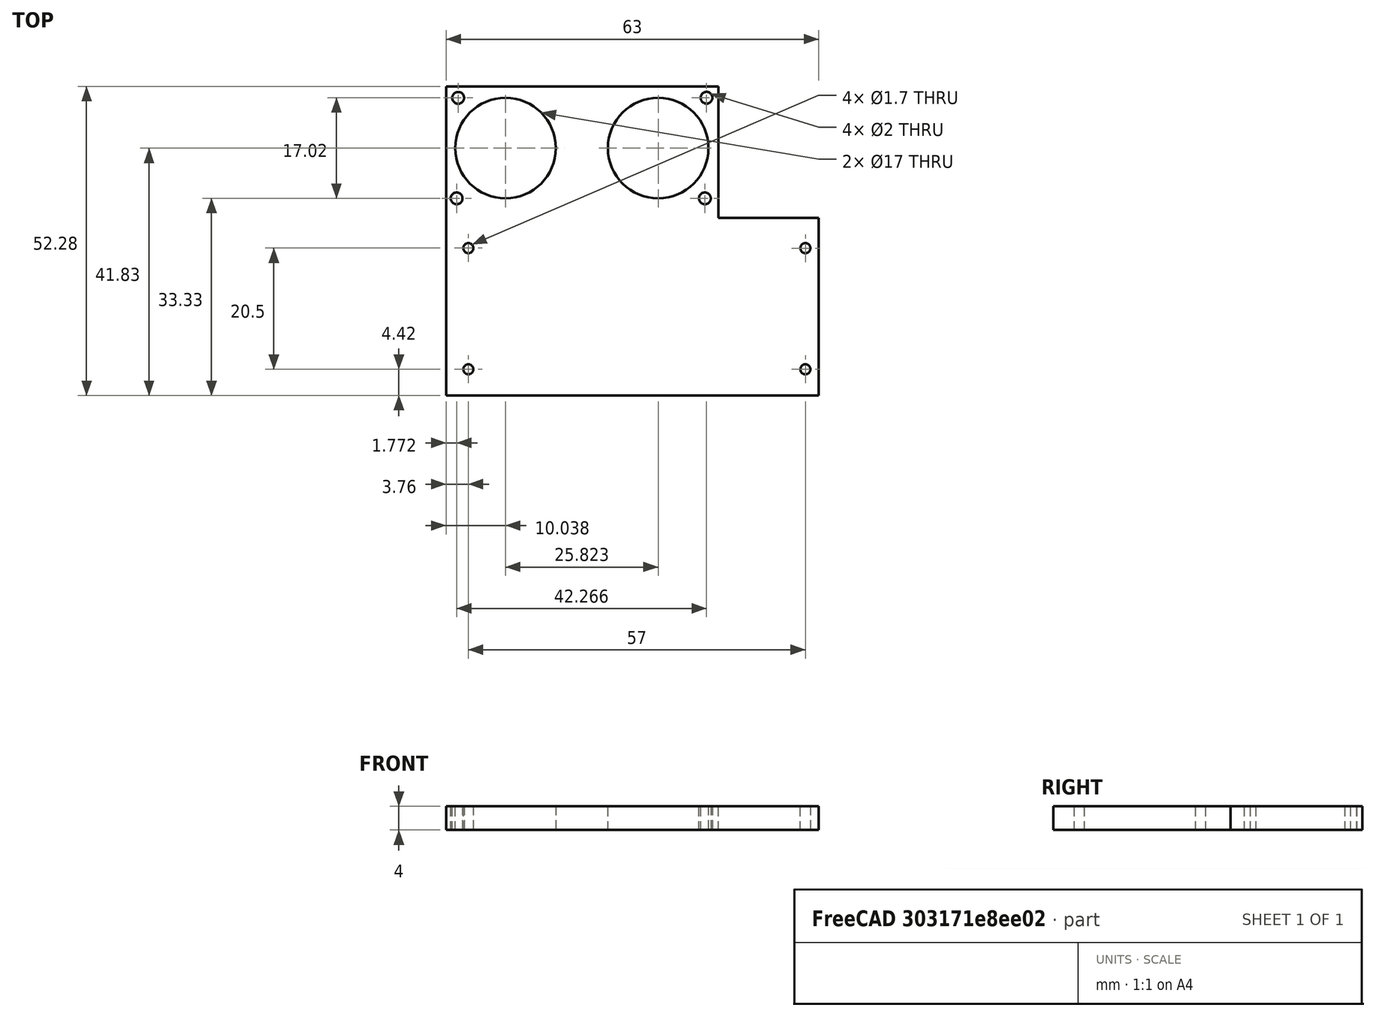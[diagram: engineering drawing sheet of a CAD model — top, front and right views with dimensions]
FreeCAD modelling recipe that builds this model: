
FCSTD DOCUMENT  (FreeCAD 1.0RUnknown)
Label: ultrasonic_holder
License: All rights reserved
LicenseURL: https://en.wikipedia.org/wiki/All_rights_reserved
objects: Sketcher::SketchObject×3, PartDesign::Pocket×2, Mesh::Feature×1, PartDesign::Pad×1, PartDesign::Body×1
note: 16 computed .brp shape members not serialized (recipe doc carries the construction recipe); baked Part::Feature solids carry a one-line shape summary decoded from their .brp

FEATURE [Mesh::Feature] ultrasonic_holder_v3  label="ultrasonic holder v3"
FEATURE [Sketcher::SketchObject] Sketch
  ArcFitTolerance = 1e-06
  FullyConstrained = false
  MakeInternals = false
  sketch-geometry (9):
    g0: LineSegment StartX=-1.10876 StartY=-16.1017 StartZ=0 EndX=-1.10876 EndY=-25.1017 EndZ=0
    g1: LineSegment StartX=-1.10876 StartY=-25.1017 StartZ=0 EndX=34.8912 EndY=-25.1017 EndZ=0
    g2: LineSegment StartX=34.8912 StartY=-25.1017 StartZ=0 EndX=34.8912 EndY=-16.1017 EndZ=0
    g3: LineSegment StartX=34.8912 StartY=-16.1017 StartZ=0 EndX=-1.10876 EndY=-16.1017 EndZ=0
    g4: LineSegment StartX=-1.32171 StartY=-38.5763 StartZ=0 EndX=34.9013 EndY=-38.5763 EndZ=0
    g5: LineSegment StartX=34.9013 StartY=-29.5763 StartZ=0 EndX=-1.32171 EndY=-29.5763 EndZ=0
    g6: LineSegment StartX=-1.32171 StartY=-38.5763 StartZ=0 EndX=-1.32171 EndY=-29.5763 EndZ=0
    g7: LineSegment StartX=-1.10876 StartY=-25.1017 StartZ=0 EndX=34.8912 EndY=-25.1017 EndZ=0
    g8: LineSegment StartX=34.9013 StartY=-29.5763 StartZ=0 EndX=34.9013 EndY=-38.5763 EndZ=0
  constraints (18):
    c: Vertical(g0)
    c: Vertical(g2)
    c: Horizontal(g1)
    c: Horizontal(g3)
    c: Distance(g0,g2) = 36
    c: Distance(g1,g3) = 9
    c: Horizontal(g4)
    c: Horizontal(g5)
    c: Distance(g4,g5) = 9
    c: Coincident(g6,g4)
    c: Coincident(g6,g5)
    c: Vertical(g6)
    c: Coincident(g7,g0)
    c: Coincident(g7,g2)
    c: Horizontal(g7)
    c: Coincident(g8,g5)
    c: Coincident(g8,g4)
    c: Vertical(g8)
FEATURE [Sketcher::SketchObject] Sketch001
  ArcFitTolerance = 1e-06
  FullyConstrained = false
  MakeInternals = false
  sketch-geometry (8):
    g0: LineSegment StartX=-22.7673 StartY=-11.8529 StartZ=0 EndX=-22.7673 EndY=-41.8529 EndZ=0
    g1: LineSegment StartX=-22.7673 StartY=-41.8529 StartZ=0 EndX=40.2327 EndY=-41.8529 EndZ=0
    g2: LineSegment StartX=40.2327 StartY=-41.8529 StartZ=0 EndX=40.2327 EndY=-11.8529 EndZ=0
    g3: LineSegment StartX=23.2683 StartY=10.4306 StartZ=0 EndX=-22.7673 EndY=10.4306 EndZ=0
    g4: LineSegment StartX=-22.7673 StartY=-11.8529 StartZ=0 EndX=-22.7673 EndY=10.4306 EndZ=0
    g5: LineSegment StartX=23.2683 StartY=10.4306 StartZ=0 EndX=23.2683 EndY=-11.8529 EndZ=0
    g6: LineSegment StartX=23.2683 StartY=-11.8529 StartZ=0 EndX=40.2327 EndY=-11.8529 EndZ=0
    g7: GeomPoint X=-20.7673 Y=8.4306 Z=0
  constraints (17):
    c: Coincident(g0,g1)
    c: Coincident(g1,g2)
    c: Vertical(g0)
    c: Vertical(g2)
    c: Distance(g0,g2) = 63
    c: Distance(g1,g0) = 30
    c: Horizontal(g3)
    c: Coincident(g4,g0)
    c: Coincident(g4,g3)
    c: Vertical(g4)
    c: Coincident(g5,g3)
    c: Vertical(g5)
    c: Coincident(g6,g5)
    c: Coincident(g6,g2)
    c: Horizontal(g6)
    c: DistanceX(g3,g7) = 2
    c: DistanceY(g7,g3) = 2
FEATURE [PartDesign::Pad] Pad
  Direction = (0,0,1)
  Length = 4
  Length2 = 10
  Profile = -> Sketch001
  ReferenceAxis = -> Sketch001 [N_Axis]
  Refine = true
  Suppressed = false
  Type = 0
FEATURE [Sketcher::SketchObject] Sketch002
  ArcFitTolerance = 1e-06
  FullyConstrained = false
  MakeInternals = false
  sketch-geometry (10):
    g0: Circle CenterX=-20.7317 CenterY=8.47985 CenterZ=0 NormalX=0 NormalY=0 NormalZ=1 AngleXU=0 Radius=1
    g1: Circle CenterX=-20.998 CenterY=-8.52015 CenterZ=0 NormalX=0 NormalY=0 NormalZ=1 AngleXU=0 Radius=1
    g2: Circle CenterX=20.9912 CenterY=-8.52015 CenterZ=0 NormalX=0 NormalY=0 NormalZ=1 AngleXU=0 Radius=1
    g3: Circle CenterX=21.2683 CenterY=8.5 CenterZ=0 NormalX=0 NormalY=0 NormalZ=1 AngleXU=0 Radius=1
    g4: Circle CenterX=37.9897 CenterY=-16.9346 CenterZ=0 NormalX=0 NormalY=0 NormalZ=1 AngleXU=0 Radius=0.85
    g5: Circle CenterX=37.9897 CenterY=-37.4301 CenterZ=0 NormalX=0 NormalY=0 NormalZ=1 AngleXU=0 Radius=0.85
    g6: Circle CenterX=-19.0103 CenterY=-37.4301 CenterZ=0 NormalX=0 NormalY=0 NormalZ=1 AngleXU=0 Radius=0.85
    g7: Circle CenterX=-19.0103 CenterY=-16.9301 CenterZ=0 NormalX=0 NormalY=0 NormalZ=1 AngleXU=0 Radius=0.85
    g8: Circle CenterX=-12.7317 CenterY=-0.0201493 CenterZ=0 NormalX=0 NormalY=0 NormalZ=1 AngleXU=0 Radius=8.5
    g9: Circle CenterX=13.0912 CenterY=-0.0201493 CenterZ=0 NormalX=0 NormalY=0 NormalZ=1 AngleXU=0 Radius=8.5
  constraints (20):
    c: Diameter(g0) = 2
    c: Diameter(g1) = 2
    c: Diameter(g2) = 2
    c: Diameter(g3) = 2
    c: Diameter(g4) = 1.7
    c: Diameter(g5) = 1.7
    c: Diameter(g7) = 1.7
    c: Diameter(g8) = 17
    c: Diameter(g9) = 17
    c: DistanceX(g0,g3) = 42
    c: DistanceX(g0,g8) = 8
    c: DistanceY(g8,g0) = 8.5
    c: DistanceY(g9,g0) = 8.5
    c: DistanceY(g1,g0) = 17
    c: DistanceY(g2,g0) = 17
    c: DistanceY(g7,g1) = 8.41
    c: DistanceY(g6,g7) = 20.5
    c: DistanceY(g5,g7) = 20.5
    c: DistanceX(g7,g4) = 57
    c: DistanceX(g6,g5) = 57
FEATURE [PartDesign::Pocket] Pocket
  BaseFeature = -> Pad
  Direction = (0,0,-1)
  Length = 10
  Length2 = 5
  Midplane = true
  Profile = -> Sketch002
  ReferenceAxis = -> Sketch002 [N_Axis]
  Refine = true
  Suppressed = false
  Type = 0
FEATURE [PartDesign::Pocket] Pocket001
  BaseFeature = -> Pocket
  Direction = (1,1,1)
  Length = 5
  Length2 = 5
  Profile = -> Sketch
  ReferenceAxis = -> Sketch [N_Axis]
  Refine = true
  Suppressed = false
  Type = 0
FEATURE [PartDesign::Body] Body
  AllowCompound = false
  Group = -> [Sketch001,Sketch,Pad,Sketch002,Pocket,Pocket001]
  Origin = -> Origin
  Tip = -> Pocket001
